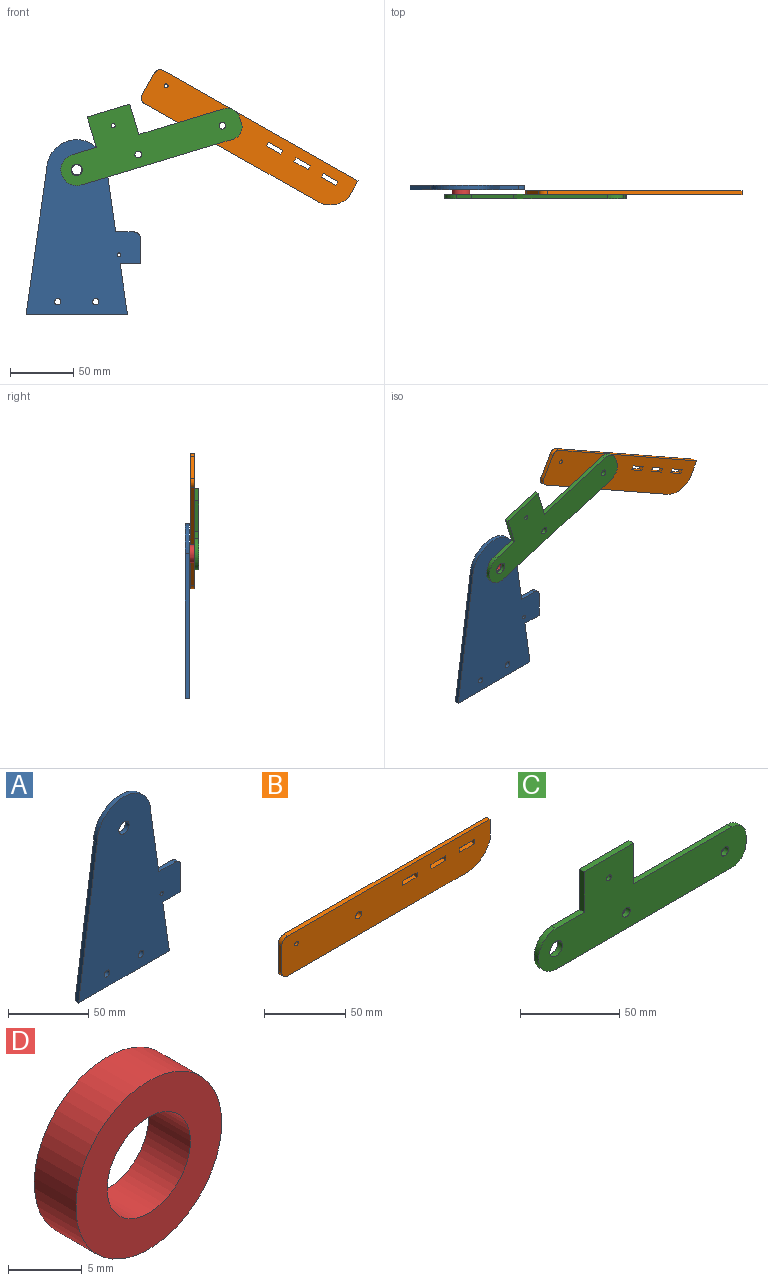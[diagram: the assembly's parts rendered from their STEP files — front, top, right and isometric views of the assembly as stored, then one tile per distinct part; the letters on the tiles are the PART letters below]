
ASSEMBLY  parts=4 mates=3
PART A: 15 faces, bbox 90.3x3.2x137.7 mm
  f0: plane 20x3.2mm, normal (1,0,0), area 64mm2, adj f11,f12,f13,f14
  f1: plane 14.57x3.2mm, normal (0,0,1), area 46.6mm2, adj f2,f12,f13,f14
  f2: plane 49x7mm, normal (0.99,0,0.14), area 158.4mm2, adj f1,f3,f12,f13
  f3: cylinder r=23.71mm len=47.43mm, axis (0,1,0), area 238.4mm2, adj f2,f4,f12,f13
  f4: plane 114x16.29mm, normal (-0.99,0,0.14), area 368.5mm2, adj f3,f5,f12,f13
  f5: plane 80x3.2mm, normal (0,0,-1), area 256mm2, adj f4,f6,f12,f13
  f6: plane 40x5.71mm, normal (0.99,0,0.14), area 129.3mm2, adj f5,f11,f12,f13
  f7: cylinder r=4.5mm len=9mm, axis (0,1,0), area 90.5mm2, adj f12,f13
  f8: cylinder r=2.5mm len=5mm, axis (0,1,0), area 50.3mm2, adj f12,f13
  f9: cylinder r=2.5mm len=5mm, axis (0,1,0), area 50.3mm2, adj f12,f13
  f10: cylinder r=1.5mm len=3.2mm, axis (0,1,0), area 30.2mm2, adj f12,f13
  f11: plane 16x3.2mm, normal (0,0,-1), area 51.2mm2, adj f0,f6,f12,f13
  f12: plane 137.71x90.29mm, normal (0,-1,0), area 8476.1mm2, adj f0,f1,f2,f3,f4,f5,f6,f7
  f13: plane 137.71x90.29mm, normal (0,1,0), area 8476.1mm2, adj f0,f1,f2,f3,f4,f5,f6,f7
  f14: cylinder r=5mm len=5mm, axis (0,1,0), area 25.1mm2, adj f0,f1,f12,f13
PART B: 23 faces, bbox 181.5x3.2x30 mm
  f0: plane 156.5x3.2mm, normal (0,0,-1), area 500.8mm2, adj f1,f19,f20,f22
  f1: cylinder r=20.83mm len=20mm, axis (0,1,0), area 85.8mm2, adj f0,f2,f19,f20
  f2: plane 15x3.2mm, normal (1,0,0), area 48mm2, adj f1,f3,f19,f20
  f3: plane 176.5x3.2mm, normal (0,0,1), area 564.8mm2, adj f2,f19,f20,f21
  f4: plane 13x3.2mm, normal (0,0,1), area 41.6mm2, adj f5,f13,f19,f20
  f5: plane 3.4x3.2mm, normal (1,0,0), area 10.9mm2, adj f4,f6,f19,f20
  f6: plane 13x3.2mm, normal (0,0,-1), area 41.6mm2, adj f5,f13,f19,f20
  f7: plane 3.4x3.2mm, normal (-1,0,0), area 10.9mm2, adj f8,f14,f19,f20
  f8: plane 13x3.2mm, normal (0,0,1), area 41.6mm2, adj f7,f9,f19,f20
  f9: plane 3.4x3.2mm, normal (1,0,0), area 10.9mm2, adj f8,f14,f19,f20
  f10: plane 3.4x3.2mm, normal (1,0,0), area 10.9mm2, adj f11,f15,f19,f20
  f11: plane 13x3.2mm, normal (0,0,-1), area 41.6mm2, adj f10,f12,f19,f20
  f12: plane 3.4x3.2mm, normal (-1,0,0), area 10.9mm2, adj f11,f15,f19,f20
  f13: plane 3.4x3.2mm, normal (-1,0,0), area 10.9mm2, adj f4,f6,f19,f20
  f14: plane 13x3.2mm, normal (0,0,-1), area 41.6mm2, adj f7,f9,f19,f20
  f15: plane 13x3.2mm, normal (0,0,1), area 41.6mm2, adj f10,f12,f19,f20
  f16: cylinder r=2.6mm len=5.2mm, axis (0,1,0), area 52.3mm2, adj f19,f20
  f17: cylinder r=1.6mm len=3.2mm, axis (0,1,0), area 32.2mm2, adj f19,f20
  f18: plane 20x3.2mm, normal (-1,0,0), area 64mm2, adj f19,f20,f21,f22
  f19: plane 181.5x30mm, normal (0,-1,0), area 5193.4mm2, adj f0,f1,f2,f3,f4,f5,f6,f7
  f20: plane 181.5x30mm, normal (0,1,0), area 5193.4mm2, adj f0,f1,f2,f3,f4,f5,f6,f7
  f21: cylinder r=5mm len=5mm, axis (0,1,0), area 25.1mm2, adj f3,f18,f19,f20
  f22: cylinder r=5mm len=5mm, axis (0,-1,0), area 25.1mm2, adj f0,f18,f19,f20
PART C: 16 faces, bbox 147.5x3.2x50 mm
  f0: plane 25x3.2mm, normal (-1,0,0), area 80mm2, adj f1,f11,f12,f13
  f1: plane 20x3.2mm, normal (0,0,1), area 64mm2, adj f0,f2,f12,f13
  f2: cylinder r=12.5mm len=25mm, axis (0,1,0), area 125.7mm2, adj f1,f3,f12,f13
  f3: plane 125x3.2mm, normal (0,0,-1), area 400mm2, adj f2,f12,f13,f14
  f4: plane 5x3.2mm, normal (1,0,0), area 16mm2, adj f12,f13,f14,f15
  f5: plane 70x3.2mm, normal (0,0,1), area 224mm2, adj f6,f12,f13,f15
  f6: plane 25x3.2mm, normal (1,0,0), area 80mm2, adj f5,f11,f12,f13
  f7: cylinder r=4.5mm len=9mm, axis (0,1,0), area 90.5mm2, adj f12,f13
  f8: cylinder r=2.6mm len=5.2mm, axis (0,1,0), area 52.3mm2, adj f12,f13
  f9: cylinder r=2.7mm len=5.4mm, axis (0,1,0), area 54.3mm2, adj f12,f13
  f10: cylinder r=1.6mm len=3.2mm, axis (0,1,0), area 32.2mm2, adj f12,f13
  f11: plane 35x3.2mm, normal (0,0,1), area 112mm2, adj f0,f6,f12,f13
  f12: plane 147.5x50mm, normal (0,-1,0), area 4336.7mm2, adj f0,f1,f2,f3,f4,f5,f6,f7
  f13: plane 147.5x50mm, normal (0,1,0), area 4336.7mm2, adj f0,f1,f2,f3,f4,f5,f6,f7
  f14: cylinder r=10mm len=10mm, axis (0,-1,0), area 50.3mm2, adj f3,f4,f12,f13
  f15: cylinder r=10mm len=10mm, axis (0,-1,0), area 50.3mm2, adj f4,f5,f12,f13
PART D: 4 faces, bbox 14x4x14 mm
  f0: cylinder r=4mm len=8mm, axis (0,-1,0), area 100.5mm2, adj f2,f3
  f1: cylinder r=7mm len=14mm, axis (0,-1,0), area 175.9mm2, adj f2,f3
  f2: plane 14x14mm, normal (0,1,0), area 103.7mm2, adj f0,f1
  f3: plane 14x14mm, normal (0,-1,0), area 103.7mm2, adj f0,f1
PLACE A t=(-17.59,86.2,-39.09)mm fixed
PLACE B rot(axis=(0,1,0),29.5deg) t=(140.28,82.2,15.24)mm
PLACE C rot(axis=(0,-1,0),16.8deg) t=(39.84,79,22.27)mm
PLACE D t=(-18.16,79,4.91)mm
MATE revolute D.f0 <-> C.f2  axis (0,-1,0) through (-17.59,79,4.91)mm
MATE revolute C.f8 <-> B.f16  axis (0,1,0) through (97.28,79,39.62)mm
MATE fastened A.f7 <-> D.f0  axis (0,-1,0) through (-17.59,83,4.91)mm
